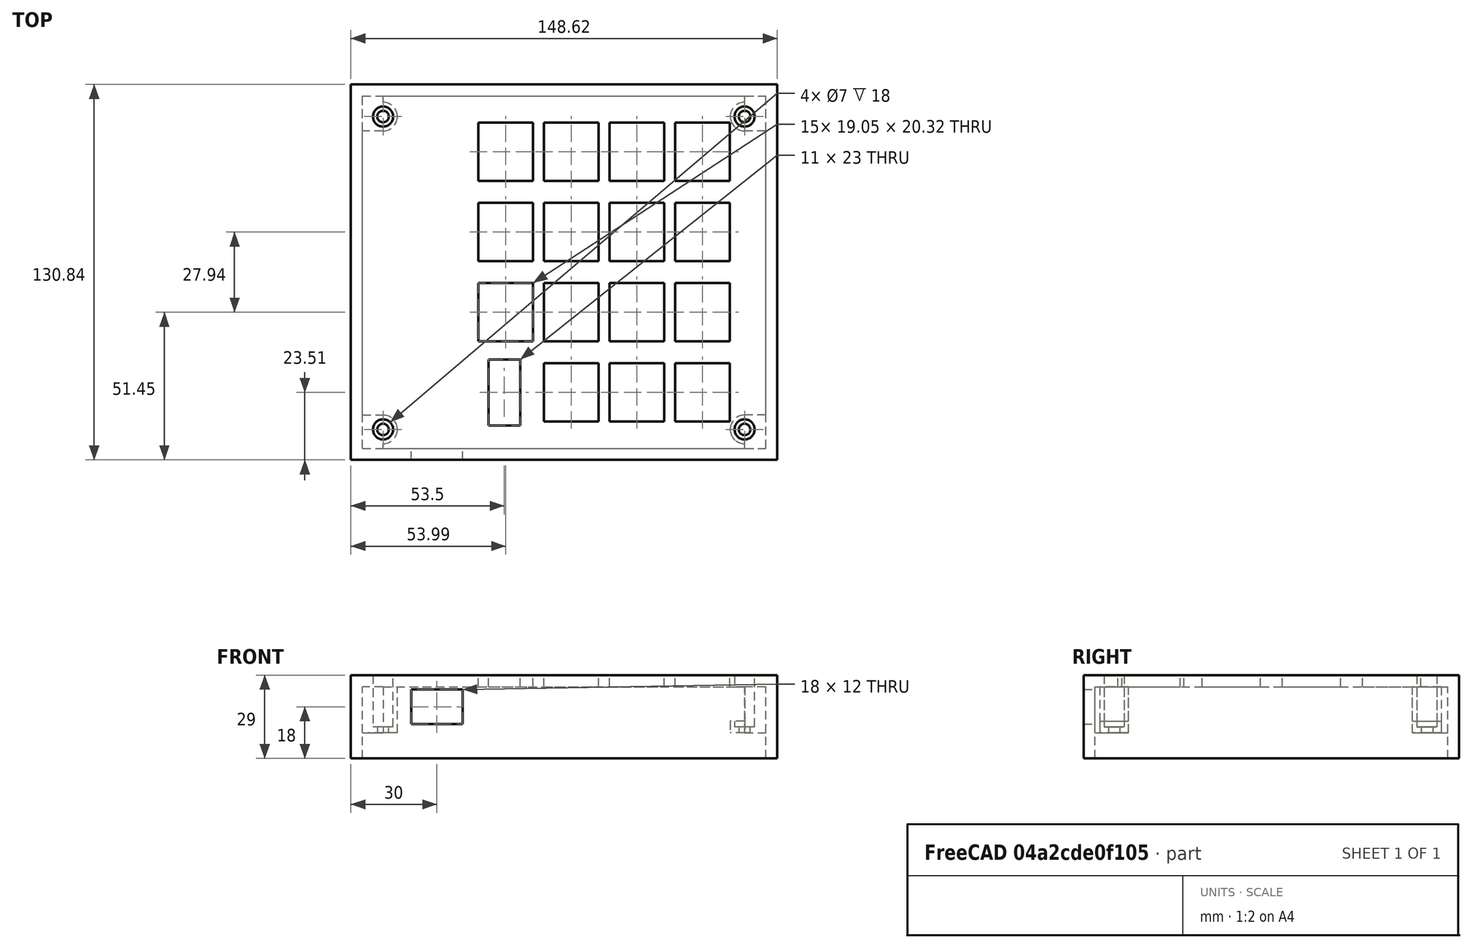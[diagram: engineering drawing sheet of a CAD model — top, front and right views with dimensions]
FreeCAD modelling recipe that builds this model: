
FCSTD DOCUMENT  (FreeCAD 0.20R29410 (Git))
Label: HIDPanelCover
License: All rights reserved
LicenseURL: http://en.wikipedia.org/wiki/All_rights_reserved
objects: Part::Box×25, Part::Cylinder×12, Part::Cut×2, Part::MultiFuse×2, Spreadsheet::Sheet×1
note: 41 computed .brp shape members not serialized (recipe doc carries the construction recipe); baked Part::Feature solids carry a one-line shape summary decoded from their .brp

FEATURE [Spreadsheet::Sheet] Spreadsheet  label="SS"
  cells = A2=PCBWidth; B2(PCBWidth)==116.84mm; A3=PCBLength; B3(PCBLength)==134.62mm; A4=PCBSpacing; B4(PCBSpacing)==3mm; A5=PCBThickness; B5(PCBThickness)==1.6mm; A6=CoverHeight; B6(CoverHeight)==25mm; A7=CaseThickness; B7(CaseThickness)==4mm; A9=StandOffOD; B9(StandOffOD)==10mm; A10=StandOffID; B10(StandOffID)==7mm; A11=StandOfHeight; B11(StandOffHeight)==20mm; A12=StandOffHoleDiameter; B12(StandOffHoleDiameter)==4mm; A13=StandOffBottomThickness; B13(StandOffBottomThickness)==2mm; A15=StandOff1X; B15(StandOff1X)==22mm - 17.78mm; A16=StandOff1Y; B16(StandOff1Y)==90mm - 86.36mm; A17=StandOff2X; B17(StandOff2X)==22mm - 17.78mm; A18=StandOff2Y; B18(StandOff2Y)==199mm - 86.36mm; A19=StandOff3X; B19(StandOff3X)==130.2mm; A20=StandOff3Y; B20(StandOff3Y)==3.64mm; A21=StandOff4X; B21(StandOff4X)==130.2mm; A22=StandOff4Y; B22(StandOff4Y)==112.64mm; A24=CutOut1CtrX; B24(CutOut1CtrX)==87.63mm - 17.78mm; A25=CutOut1CtrY; B25(CutOut1CtrY)==102.87mm - 86.36mm; A26=CutOut1Width; B26(CutOut1Width)==113.03mm - 92.70999999999999mm; A27=CutOut1Length; B27(CutOut1Length)==96.52mm - 77.47mm; A29=CutOut2CtrX; B29(CutOut2CtrX)==110.49mm - 17.78mm; A30=CutOut2CtrY; B30(CutOut2CtrY)==102.87mm - 86.36mm; A31=CutOut2Width; B31(CutOut2Width)==113.03mm - 92.70999999999999mm; A32=CutOut2Length; B32(CutOut2Length)==96.52mm - 77.47mm; A34=CutOut3CtrX; B34(CutOut3CtrX)==133.35mm - 17.78mm; A35=CutOut3CtrY; B35(CutOut3CtrY)==102.87mm - 86.36mm; A36=CutOut3Width; B36(CutOut3Width)==113.03mm - 92.70999999999999mm; A37=CutOut3Length; B37(CutOut3Length)==96.52mm - 77.47mm; A39=CutOut4CtrX; B39(CutOut4CtrX)==64.77mm - 17.78mm; A40=CutOut4CtrY; B40(CutOut4CtrY)==130.81mm - 86.36mm; A41=CutOut4Width; B41(CutOut4Width)==113.03mm - 92.70999999999999mm; A42=CutOut4Length; B42(CutOut4Length)==96.52mm - 77.47mm; A44=CutOut5CtrX; B44(CutOut5CtrX)==87.63mm - 17.78mm; A45=CutOut5CtrY; B45(CutOut5CtrY)==130.81mm - 86.36mm; A46=CutOut5Width; B46(CutOut5Width)==113.03mm - 92.70999999999999mm; A47=CutOut5Length; B47(CutOut5Length)==96.52mm - 77.47mm; A49=CutOut6CtrX; B49(CutOut6CtrX)==110.49mm - 17.78mm; A50=CutOut6CtrY; B50(CutOut6CtrY)==130.81mm - 86.36mm; A51=CutOut6Width; B51(CutOut6Width)==113.03mm - 92.70999999999999mm; A52=CutOut6Length; B52(CutOut6Length)==96.52mm - 77.47mm; A54=CutOut7CtrX; B54(CutOut7CtrX)==133.35mm - 17.78mm; A55=CutOut7CtrY; B55(CutOut7CtrY)==130.81mm - 86.36mm; A56=CutOut7Width; B56(CutOut7Width)==113.03mm - 92.70999999999999mm; A57=CutOut7Length; B57(CutOut7Length)==96.52mm - 77.47mm; A59=CutOut8CtrX; B59(CutOut8CtrX)==64.77mm - 17.78mm; A60=CutOut8CtrY; B60(CutOut8CtrY)==158.75mm - 86.36mm; A61=CutOut8Width; B61(CutOut8Width)==113.03mm - 92.70999999999999mm; A62=CutOut8Length; B62(CutOut8Length)==96.52mm - 77.47mm; A64=CutOut9CtrX; B64(CutOut9CtrX)==87.63mm - 17.78mm; A65=CutOut9CtrY; B65(CutOut9CtrY)==158.75mm - 86.36mm; A66=CutOut9Width; B66(CutOut9Width)==113.03mm - 92.70999999999999mm; A67=CutOut9Length; B67(CutOut9Length)==96.52mm - 77.47mm; A69=CutOut10CtrX; B69(CutOut10CtrX)==110.49mm - 17.78mm; A70=CutOut10CtrY; B70(CutOut10CtrY)==158.75mm - 86.36mm; A71=CutOut10Width; B71(CutOut10Width)==113.03mm - 92.70999999999999mm; A72=CutOut10Length; B72(CutOut10Length)==96.52mm - 77.47mm; A74=CutOut11CtrX; B74(CutOut11CtrX)==133.35mm - 17.78mm; A75=CutOut11CtrY; B75(CutOut11CtrY)==158.75mm - 86.36mm; A76=CutOut11Width; B76(CutOut11Width)==113.03mm - 92.70999999999999mm; A77=CutOut11Length; B77(CutOut11Length)==96.52mm - 77.47mm; A79=CutOut12CtrX; B79(CutOut12CtrX)==64.77mm - 17.78mm; A80=CutOut12CtrY; B80(CutOut12CtrY)==186.69mm - 86.36mm; A81=CutOut12Width; B81(CutOut12Width)==113.03mm - 92.70999999999999mm; A82=CutOut12Length; B82(CutOut12Length)==96.52mm - 77.47mm; A84=CutOut13CtrX; B84(CutOut13CtrX)==87.63mm - 17.78mm; A85=CutOut13CtrY; B85(CutOut13CtrY)==186.69mm - 86.36mm; A86=CutOut13Width; B86(CutOut13Width)==113.03mm - 92.70999999999999mm; A87=CutOut13Length; B87(CutOut13Length)==96.52mm - 77.47mm; A89=CutOut14CtrX; B89(CutOut14CtrX)==110.49mm - 17.78mm; A90=CutOut14CtrY; B90(CutOut14CtrY)==186.69mm - 86.36mm; A91=CutOut14Width; B91(CutOut14Width)==113.03mm - 92.70999999999999mm; A92=CutOut14Length; B92(CutOut14Length)==96.52mm - 77.47mm; A94=CutOut15CtrX; B94(CutOut15CtrX)==133.35mm - 17.78mm; A95=CutOut15CtrY; B95(CutOut15CtrY)==186.69mm - 86.36mm; A96=CutOut15Width; B96(CutOut15Width)==113.03mm - 92.70999999999999mm; A97=CutOut15Length; B97(CutOut15Length)==96.52mm - 77.47mm; A99=LEDCutOutCtrX; B99(LEDCutOutCtrX)==46.5mm; A100=LEDCutOutCtrY; B100(LEDCutOutCtrY)==16.51mm; A101=LEDCutOutWidth; B101(LEDCutOutWidth)==23mm; A102=LEDCutOutLength; B102(LEDCutOutLength)==11mm; A104=CableCutOutZ; B104(CableCutOutZ)==18mm; A105=CableCutOutX; B105(CableCutOutX)==23mm; A106=CableCutOutHeight; B106(CableCutOutHeight)==12mm; A107=CableCutOutLength; B107(CableCutOutLength)==18mm
FEATURE [Part::Box] Box  label="BodyBulk"
  AttacherType = Attacher::AttachEngine3D
  Height = 29
  Length = 148.62
  Placement = pos=(-7,-7,-25) rot=(0,0,1;0rad)
  Width = 130.84
  expr: .Placement.Base.x = -<<SS>>.CaseThickness - <<SS>>.PCBSpacing
  expr: .Placement.Base.y = -<<SS>>.CaseThickness - <<SS>>.PCBSpacing
  expr: .Placement.Base.z = -<<SS>>.CoverHeight
  expr: Height = <<SS>>.CoverHeight + <<SS>>.CaseThickness
  expr: Length = <<SS>>.PCBLength + 2 * (<<SS>>.CaseThickness + <<SS>>.PCBSpacing)
  expr: Width = <<SS>>.PCBWidth + 2 * (<<SS>>.CaseThickness + <<SS>>.PCBSpacing)
FEATURE [Part::Box] Box001  label="BodyInside"
  AttacherType = Attacher::AttachEngine3D
  Height = 25
  Length = 140.62
  Placement = pos=(-3,-3,-25) rot=(0,0,1;0rad)
  Width = 122.84
  expr: .Placement.Base.x = -<<SS>>.PCBSpacing
  expr: .Placement.Base.y = -<<SS>>.PCBSpacing
  expr: .Placement.Base.z = -<<SS>>.CoverHeight
  expr: Height = <<SS>>.CoverHeight
  expr: Length = <<SS>>.PCBLength + 2 * <<SS>>.PCBSpacing
  expr: Width = <<SS>>.PCBWidth + 2 * <<SS>>.PCBSpacing
FEATURE [Part::Cut] Cut  label="BoxWall"
  Base = -> Box
  Tool = -> Box001
FEATURE [Part::Cylinder] Cylinder  label="StandOff1Hole"
  Angle = 360
  AttacherType = Attacher::AttachEngine3D
  FirstAngle = 0
  Height = 20
  Placement = pos=(4.22,3.64,-16) rot=(0,0,1;0rad)
  Radius = 2
  SecondAngle = 0
  expr: .Placement.Base.x = <<SS>>.StandOff1X
  expr: .Placement.Base.y = <<SS>>.StandOff1Y
  expr: .Placement.Base.z = <<SS>>.CaseThickness - <<SS>>.StandOffHeight
  expr: Height = <<SS>>.StandOffHeight
  expr: Radius = <<SS>>.StandOffHoleDiameter / 2
FEATURE [Part::Cylinder] Cylinder001  label="StandOff1ID"
  Angle = 360
  AttacherType = Attacher::AttachEngine3D
  FirstAngle = 0
  Height = 18
  Placement = pos=(4.22,3.64,-14) rot=(0,0,1;0rad)
  Radius = 3.5
  SecondAngle = 0
  expr: .Placement.Base.x = <<SS>>.StandOff1X
  expr: .Placement.Base.y = <<SS>>.StandOff1Y
  expr: .Placement.Base.z = <<SS>>.CaseThickness - <<SS>>.StandOffHeight + <<SS>>.StandOffBottomThickness
  expr: Height = <<SS>>.StandOffHeight - <<SS>>.StandOffBottomThickness
  expr: Radius = <<SS>>.StandOffID / 2
FEATURE [Part::Cylinder] Cylinder002  label="StandOff1OD"
  Angle = 360
  AttacherType = Attacher::AttachEngine3D
  FirstAngle = 0
  Height = 20
  Placement = pos=(4.22,3.64,-16) rot=(0,0,1;0rad)
  Radius = 5
  SecondAngle = 0
  expr: .Placement.Base.x = <<SS>>.StandOff1X
  expr: .Placement.Base.y = <<SS>>.StandOff1Y
  expr: .Placement.Base.z = <<SS>>.CaseThickness - <<SS>>.StandOffHeight
  expr: Height = <<SS>>.StandOffHeight
  expr: Radius = <<SS>>.StandOffOD / 2
FEATURE [Part::Cylinder] Cylinder003  label="StandOff2OD"
  Angle = 360
  AttacherType = Attacher::AttachEngine3D
  FirstAngle = 0
  Height = 20
  Placement = pos=(4.22,112.64,-16) rot=(0,0,1;0rad)
  Radius = 5
  SecondAngle = 0
  expr: .Placement.Base.x = <<SS>>.StandOff2X
  expr: .Placement.Base.y = <<SS>>.StandOff2Y
  expr: .Placement.Base.z = <<SS>>.CaseThickness - <<SS>>.StandOffHeight
  expr: Height = <<SS>>.StandOffHeight
  expr: Radius = <<SS>>.StandOffOD / 2
FEATURE [Part::Cylinder] Cylinder004  label="StandOff2Hole"
  Angle = 360
  AttacherType = Attacher::AttachEngine3D
  FirstAngle = 0
  Height = 20
  Placement = pos=(4.22,112.64,-16) rot=(0,0,1;0rad)
  Radius = 2
  SecondAngle = 0
  expr: .Placement.Base.x = <<SS>>.StandOff2X
  expr: .Placement.Base.y = <<SS>>.StandOff2Y
  expr: .Placement.Base.z = <<SS>>.CaseThickness - <<SS>>.StandOffHeight
  expr: Height = <<SS>>.StandOffHeight
  expr: Radius = <<SS>>.StandOffHoleDiameter / 2
FEATURE [Part::Cylinder] Cylinder005  label="StandOff2ID"
  Angle = 360
  AttacherType = Attacher::AttachEngine3D
  FirstAngle = 0
  Height = 18
  Placement = pos=(4.22,112.64,-14) rot=(0,0,1;0rad)
  Radius = 3.5
  SecondAngle = 0
  expr: .Placement.Base.x = <<SS>>.StandOff2X
  expr: .Placement.Base.y = <<SS>>.StandOff2Y
  expr: .Placement.Base.z = <<SS>>.CaseThickness - <<SS>>.StandOffHeight + <<SS>>.StandOffBottomThickness
  expr: Height = <<SS>>.StandOffHeight - <<SS>>.StandOffBottomThickness
  expr: Radius = <<SS>>.StandOffID / 2
FEATURE [Part::Box] Box004  label="ControlCutOut1"
  AttacherType = Attacher::AttachEngine3D
  Height = 4
  Length = 19.05
  Placement = pos=(60.325,6.35,0) rot=(0,0,1;0rad)
  Width = 20.32
  expr: .Placement.Base.x = <<SS>>.CutOut1CtrX - <<SS>>.CutOut1Length / 2
  expr: .Placement.Base.y = <<SS>>.CutOut1CtrY - <<SS>>.CutOut1Width / 2
  expr: .Placement.Base.z = 0mm
  expr: Height = <<SS>>.CaseThickness
  expr: Length = <<SS>>.CutOut1Length
  expr: Width = <<SS>>.CutOut1Width
FEATURE [Part::Box] Box005  label="ControlCutOut2"
  AttacherType = Attacher::AttachEngine3D
  Height = 4
  Length = 19.05
  Placement = pos=(83.185,6.35,0) rot=(0,0,1;0rad)
  Width = 20.32
  expr: .Placement.Base.x = <<SS>>.CutOut2CtrX - <<SS>>.CutOut2Length / 2
  expr: .Placement.Base.y = <<SS>>.CutOut2CtrY - <<SS>>.CutOut2Width / 2
  expr: .Placement.Base.z = 0mm
  expr: Height = <<SS>>.CaseThickness
  expr: Length = <<SS>>.CutOut2Length
  expr: Width = <<SS>>.CutOut2Width
FEATURE [Part::Box] Box006  label="ControlCutOut3"
  AttacherType = Attacher::AttachEngine3D
  Height = 4
  Length = 19.05
  Placement = pos=(106.045,6.35,0) rot=(0,0,1;0rad)
  Width = 20.32
  expr: .Placement.Base.x = <<SS>>.CutOut3CtrX - <<SS>>.CutOut3Length / 2
  expr: .Placement.Base.y = <<SS>>.CutOut3CtrY - <<SS>>.CutOut3Width / 2
  expr: .Placement.Base.z = 0mm
  expr: Height = <<SS>>.CaseThickness
  expr: Length = <<SS>>.CutOut3Length
  expr: Width = <<SS>>.CutOut3Width
FEATURE [Part::Box] Box007  label="ControlCutOut4"
  AttacherType = Attacher::AttachEngine3D
  Height = 4
  Length = 19.05
  Placement = pos=(37.465,34.29,0) rot=(0,0,1;0rad)
  Width = 20.32
  expr: .Placement.Base.x = <<SS>>.CutOut4CtrX - <<SS>>.CutOut4Length / 2
  expr: .Placement.Base.y = <<SS>>.CutOut4CtrY - <<SS>>.CutOut4Width / 2
  expr: .Placement.Base.z = 0mm
  expr: Height = <<SS>>.CaseThickness
  expr: Length = <<SS>>.CutOut4Length
  expr: Width = <<SS>>.CutOut4Width
FEATURE [Part::Box] Box008  label="ControlCutOut5"
  AttacherType = Attacher::AttachEngine3D
  Height = 4
  Length = 19.05
  Placement = pos=(60.325,34.29,0) rot=(0,0,1;0rad)
  Width = 20.32
  expr: .Placement.Base.x = <<SS>>.CutOut5CtrX - <<SS>>.CutOut5Length / 2
  expr: .Placement.Base.y = <<SS>>.CutOut5CtrY - <<SS>>.CutOut5Width / 2
  expr: .Placement.Base.z = 0mm
  expr: Height = <<SS>>.CaseThickness
  expr: Length = <<SS>>.CutOut5Length
  expr: Width = <<SS>>.CutOut5Width
FEATURE [Part::Box] Box009  label="ControlCutOut6"
  AttacherType = Attacher::AttachEngine3D
  Height = 4
  Length = 19.05
  Placement = pos=(83.185,34.29,0) rot=(0,0,1;0rad)
  Width = 20.32
  expr: .Placement.Base.x = <<SS>>.CutOut6CtrX - <<SS>>.CutOut6Length / 2
  expr: .Placement.Base.y = <<SS>>.CutOut6CtrY - <<SS>>.CutOut6Width / 2
  expr: .Placement.Base.z = 0mm
  expr: Height = <<SS>>.CaseThickness
  expr: Length = <<SS>>.CutOut6Length
  expr: Width = <<SS>>.CutOut6Width
FEATURE [Part::Box] Box010  label="ControlCutOut7"
  AttacherType = Attacher::AttachEngine3D
  Height = 4
  Length = 19.05
  Placement = pos=(106.045,34.29,0) rot=(0,0,1;0rad)
  Width = 20.32
  expr: .Placement.Base.x = <<SS>>.CutOut7CtrX - <<SS>>.CutOut7Length / 2
  expr: .Placement.Base.y = <<SS>>.CutOut7CtrY - <<SS>>.CutOut7Width / 2
  expr: .Placement.Base.z = 0mm
  expr: Height = <<SS>>.CaseThickness
  expr: Length = <<SS>>.CutOut7Length
  expr: Width = <<SS>>.CutOut7Width
FEATURE [Part::Box] Box011  label="ControlCutOut8"
  AttacherType = Attacher::AttachEngine3D
  Height = 4
  Length = 19.05
  Placement = pos=(37.465,62.23,0) rot=(0,0,1;0rad)
  Width = 20.32
  expr: .Placement.Base.x = <<SS>>.CutOut8CtrX - <<SS>>.CutOut8Length / 2
  expr: .Placement.Base.y = <<SS>>.CutOut8CtrY - <<SS>>.CutOut8Width / 2
  expr: .Placement.Base.z = 0mm
  expr: Height = <<SS>>.CaseThickness
  expr: Length = <<SS>>.CutOut8Length
  expr: Width = <<SS>>.CutOut8Width
FEATURE [Part::Box] Box012  label="ControlCutOut9"
  AttacherType = Attacher::AttachEngine3D
  Height = 4
  Length = 19.05
  Placement = pos=(60.325,62.23,0) rot=(0,0,1;0rad)
  Width = 20.32
  expr: .Placement.Base.x = <<SS>>.CutOut9CtrX - <<SS>>.CutOut9Length / 2
  expr: .Placement.Base.y = <<SS>>.CutOut9CtrY - <<SS>>.CutOut9Width / 2
  expr: .Placement.Base.z = 0mm
  expr: Height = <<SS>>.CaseThickness
  expr: Length = <<SS>>.CutOut9Length
  expr: Width = <<SS>>.CutOut9Width
FEATURE [Part::Box] Box013  label="ControlCutOut10"
  AttacherType = Attacher::AttachEngine3D
  Height = 4
  Length = 19.05
  Placement = pos=(83.185,62.23,0) rot=(0,0,1;0rad)
  Width = 20.32
  expr: .Placement.Base.x = <<SS>>.CutOut10CtrX - <<SS>>.CutOut10Length / 2
  expr: .Placement.Base.y = <<SS>>.CutOut10CtrY - <<SS>>.CutOut10Width / 2
  expr: .Placement.Base.z = 0mm
  expr: Height = <<SS>>.CaseThickness
  expr: Length = <<SS>>.CutOut10Length
  expr: Width = <<SS>>.CutOut10Width
FEATURE [Part::Box] Box014  label="ControlCutOut11"
  AttacherType = Attacher::AttachEngine3D
  Height = 4
  Length = 19.05
  Placement = pos=(106.045,62.23,0) rot=(0,0,1;0rad)
  Width = 20.32
  expr: .Placement.Base.x = <<SS>>.CutOut11CtrX - <<SS>>.CutOut11Length / 2
  expr: .Placement.Base.y = <<SS>>.CutOut11CtrY - <<SS>>.CutOut11Width / 2
  expr: .Placement.Base.z = 0mm
  expr: Height = <<SS>>.CaseThickness
  expr: Length = <<SS>>.CutOut11Length
  expr: Width = <<SS>>.CutOut11Width
FEATURE [Part::Box] Box015  label="ControlCutOut12"
  AttacherType = Attacher::AttachEngine3D
  Height = 4
  Length = 19.05
  Placement = pos=(37.465,90.17,0) rot=(0,0,1;0rad)
  Width = 20.32
  expr: .Placement.Base.x = <<SS>>.CutOut12CtrX - <<SS>>.CutOut12Length / 2
  expr: .Placement.Base.y = <<SS>>.CutOut12CtrY - <<SS>>.CutOut12Width / 2
  expr: .Placement.Base.z = 0mm
  expr: Height = <<SS>>.CaseThickness
  expr: Length = <<SS>>.CutOut12Length
  expr: Width = <<SS>>.CutOut12Width
FEATURE [Part::Box] Box016  label="ControlCutOut13"
  AttacherType = Attacher::AttachEngine3D
  Height = 4
  Length = 19.05
  Placement = pos=(60.325,90.17,0) rot=(0,0,1;0rad)
  Width = 20.32
  expr: .Placement.Base.x = <<SS>>.CutOut13CtrX - <<SS>>.CutOut13Length / 2
  expr: .Placement.Base.y = <<SS>>.CutOut13CtrY - <<SS>>.CutOut13Width / 2
  expr: .Placement.Base.z = 0mm
  expr: Height = <<SS>>.CaseThickness
  expr: Length = <<SS>>.CutOut13Length
  expr: Width = <<SS>>.CutOut13Width
FEATURE [Part::Box] Box017  label="ControlCutOut14"
  AttacherType = Attacher::AttachEngine3D
  Height = 4
  Length = 19.05
  Placement = pos=(83.185,90.17,0) rot=(0,0,1;0rad)
  Width = 20.32
  expr: .Placement.Base.x = <<SS>>.CutOut14CtrX - <<SS>>.CutOut14Length / 2
  expr: .Placement.Base.y = <<SS>>.CutOut14CtrY - <<SS>>.CutOut14Width / 2
  expr: .Placement.Base.z = 0mm
  expr: Height = <<SS>>.CaseThickness
  expr: Length = <<SS>>.CutOut14Length
  expr: Width = <<SS>>.CutOut14Width
FEATURE [Part::Box] Box018  label="ControlCutOut15"
  AttacherType = Attacher::AttachEngine3D
  Height = 4
  Length = 19.05
  Placement = pos=(106.045,90.17,0) rot=(0,0,1;0rad)
  Width = 20.32
  expr: .Placement.Base.x = <<SS>>.CutOut15CtrX - <<SS>>.CutOut15Length / 2
  expr: .Placement.Base.y = <<SS>>.CutOut15CtrY - <<SS>>.CutOut15Width / 2
  expr: .Placement.Base.z = 0mm
  expr: Height = <<SS>>.CaseThickness
  expr: Length = <<SS>>.CutOut15Length
  expr: Width = <<SS>>.CutOut15Width
FEATURE [Part::Box] Box019  label="LEDCutOut"
  AttacherType = Attacher::AttachEngine3D
  Height = 4
  Length = 11
  Placement = pos=(41,5.01,0) rot=(0,0,1;0rad)
  Width = 23
  expr: .Placement.Base.x = <<SS>>.LEDCutOutCtrX - <<SS>>.LEDCutOutLength / 2
  expr: .Placement.Base.y = <<SS>>.LEDCutOutCtrY - <<SS>>.LEDCutOutWidth / 2
  expr: .Placement.Base.z = 0mm
  expr: Height = <<SS>>.CaseThickness
  expr: Length = <<SS>>.LEDCutOutLength
  expr: Width = <<SS>>.LEDCutOutWidth
FEATURE [Part::Cylinder] Cylinder006  label="StandOff3OD"
  Angle = 360
  AttacherType = Attacher::AttachEngine3D
  FirstAngle = 0
  Height = 20
  Placement = pos=(130.2,3.64,-16) rot=(0,0,1;0rad)
  Radius = 5
  SecondAngle = 0
  expr: .Placement.Base.x = <<SS>>.StandOff3X
  expr: .Placement.Base.y = <<SS>>.StandOff3Y
  expr: .Placement.Base.z = <<SS>>.CaseThickness - <<SS>>.StandOffHeight
  expr: Height = <<SS>>.StandOffHeight
  expr: Radius = <<SS>>.StandOffOD / 2
FEATURE [Part::Cylinder] Cylinder007  label="StandOff4OD"
  Angle = 360
  AttacherType = Attacher::AttachEngine3D
  FirstAngle = 0
  Height = 20
  Placement = pos=(130.2,112.64,-16) rot=(0,0,1;0rad)
  Radius = 5
  SecondAngle = 0
  expr: .Placement.Base.x = <<SS>>.StandOff4X
  expr: .Placement.Base.y = <<SS>>.StandOff4Y
  expr: .Placement.Base.z = <<SS>>.CaseThickness - <<SS>>.StandOffHeight
  expr: Height = <<SS>>.StandOffHeight
  expr: Radius = <<SS>>.StandOffOD / 2
FEATURE [Part::Cylinder] Cylinder008  label="StandOff3Hole"
  Angle = 360
  AttacherType = Attacher::AttachEngine3D
  FirstAngle = 0
  Height = 20
  Placement = pos=(130.2,3.64,-16) rot=(0,0,1;0rad)
  Radius = 2
  SecondAngle = 0
  expr: .Placement.Base.x = <<SS>>.StandOff3X
  expr: .Placement.Base.y = <<SS>>.StandOff3Y
  expr: .Placement.Base.z = <<SS>>.CaseThickness - <<SS>>.StandOffHeight
  expr: Height = <<SS>>.StandOffHeight
  expr: Radius = <<SS>>.StandOffHoleDiameter / 2
FEATURE [Part::Cylinder] Cylinder009  label="StandOff4Hole"
  Angle = 360
  AttacherType = Attacher::AttachEngine3D
  FirstAngle = 0
  Height = 20
  Placement = pos=(130.2,112.64,-16) rot=(0,0,1;0rad)
  Radius = 2
  SecondAngle = 0
  expr: .Placement.Base.x = <<SS>>.StandOff4X
  expr: .Placement.Base.y = <<SS>>.StandOff4Y
  expr: .Placement.Base.z = <<SS>>.CaseThickness - <<SS>>.StandOffHeight
  expr: Height = <<SS>>.StandOffHeight
  expr: Radius = <<SS>>.StandOffHoleDiameter / 2
FEATURE [Part::Cylinder] Cylinder010  label="StandOff3ID"
  Angle = 360
  AttacherType = Attacher::AttachEngine3D
  FirstAngle = 0
  Height = 18
  Placement = pos=(130.2,3.64,-14) rot=(0,0,1;0rad)
  Radius = 3.5
  SecondAngle = 0
  expr: .Placement.Base.x = <<SS>>.StandOff3X
  expr: .Placement.Base.y = <<SS>>.StandOff3Y
  expr: .Placement.Base.z = <<SS>>.CaseThickness - <<SS>>.StandOffHeight + <<SS>>.StandOffBottomThickness
  expr: Height = <<SS>>.StandOffHeight - <<SS>>.StandOffBottomThickness
  expr: Radius = <<SS>>.StandOffID / 2
FEATURE [Part::Cylinder] Cylinder011  label="StandOff4ID"
  Angle = 360
  AttacherType = Attacher::AttachEngine3D
  FirstAngle = 0
  Height = 18
  Placement = pos=(130.2,112.64,-14) rot=(0,0,1;0rad)
  Radius = 3.5
  SecondAngle = 0
  expr: .Placement.Base.x = <<SS>>.StandOff4X
  expr: .Placement.Base.y = <<SS>>.StandOff4Y
  expr: .Placement.Base.z = <<SS>>.CaseThickness - <<SS>>.StandOffHeight + <<SS>>.StandOffBottomThickness
  expr: Height = <<SS>>.StandOffHeight - <<SS>>.StandOffBottomThickness
  expr: Radius = <<SS>>.StandOffID / 2
FEATURE [Part::Box] Box020  label="CableCutOut"
  AttacherType = Attacher::AttachEngine3D
  Height = 12
  Length = 18
  Placement = pos=(14,-7,-13) rot=(0,0,1;0rad)
  Width = 4
  expr: .Placement.Base.x = <<SS>>.CableCutOutX - <<SS>>.CableCutOutLength / 2
  expr: .Placement.Base.y = -<<SS>>.CaseThickness - <<SS>>.PCBSpacing
  expr: .Placement.Base.z = -<<SS>>.CoverHeight + <<SS>>.CableCutOutZ - <<SS>>.CableCutOutHeight / 2
  expr: Height = <<SS>>.CableCutOutHeight
  expr: Length = <<SS>>.CableCutOutLength
  expr: Width = <<SS>>.CaseThickness
FEATURE [Part::Box] Box021  label="StandOff3Remove"
  AttacherType = Attacher::AttachEngine3D
  Height = 12
  Length = 5
  Placement = pos=(125.2,-1.36,-12) rot=(0,0,1;0rad)
  Width = 10
  expr: .Placement.Base.x = <<SS>>.StandOff3X - <<SS>>.StandOffOD / 2
  expr: .Placement.Base.y = <<SS>>.StandOff3Y - <<SS>>.StandOffOD / 2
  expr: .Placement.Base.z = -<<SS>>.StandOffHeight + 2 * <<SS>>.CaseThickness
  expr: Height = <<SS>>.StandOffHeight - 2 * <<SS>>.CaseThickness
  expr: Length = <<SS>>.StandOffOD / 2
  expr: Width = <<SS>>.StandOffOD
FEATURE [Part::Box] Box022  label="StandOff4Remove"
  AttacherType = Attacher::AttachEngine3D
  Height = 12
  Length = 5
  Placement = pos=(125.2,107.64,-12) rot=(0,0,1;0rad)
  Width = 10
  expr: .Placement.Base.x = <<SS>>.StandOff4X - <<SS>>.StandOffOD / 2
  expr: .Placement.Base.y = <<SS>>.StandOff4Y - <<SS>>.StandOffOD / 2
  expr: .Placement.Base.z = -<<SS>>.StandOffHeight + 2 * <<SS>>.CaseThickness
  expr: Height = <<SS>>.StandOffHeight - 2 * <<SS>>.CaseThickness
  expr: Length = <<SS>>.StandOffOD / 2
  expr: Width = <<SS>>.StandOffOD
FEATURE [Part::MultiFuse] Fusion  label="StandOffCutOuts"
  Shapes = -> [Cylinder,Cylinder001,Cylinder004,Cylinder005,Box004,Box005,Box006,Box007,Box008,Box009,Box010,Box011,Box012,Box013,Box014,Box015,Box016,Box017,Box018,Box019,Cylinder008,Cylinder009,Cylinder010,Cylinder011,Box020,Box021,Box022]
FEATURE [Part::Box] Box023  label="StandOff1Attach"
  AttacherType = Attacher::AttachEngine3D
  Height = 20
  Length = 7.22
  Placement = pos=(-3,-3,-16) rot=(0,0,1;0rad)
  Width = 11.64
  expr: .Placement.Base.x = -<<SS>>.PCBSpacing
  expr: .Placement.Base.y = -<<SS>>.PCBSpacing
  expr: .Placement.Base.z = <<SS>>.CaseThickness - <<SS>>.StandOffHeight
  expr: Height = <<SS>>.StandOffHeight
  expr: Length = <<SS>>.StandOff1X + <<SS>>.PCBSpacing
  expr: Width = <<SS>>.StandOff1Y + <<SS>>.PCBSpacing + <<SS>>.StandOffOD / 2
FEATURE [Part::Box] Box024  label="StandOff2Attach"
  AttacherType = Attacher::AttachEngine3D
  Height = 20
  Length = 7.22
  Placement = pos=(-3,107.64,-16) rot=(0,0,1;0rad)
  Width = 12.2
  expr: .Placement.Base.x = -<<SS>>.PCBSpacing
  expr: .Placement.Base.y = <<SS>>.StandOff2Y - <<SS>>.StandOffOD / 2
  expr: .Placement.Base.z = <<SS>>.CaseThickness - <<SS>>.StandOffHeight
  expr: Height = <<SS>>.StandOffHeight
  expr: Length = <<SS>>.StandOff2X + <<SS>>.PCBSpacing
  expr: Width = <<SS>>.PCBWidth - <<SS>>.StandOff2Y + <<SS>>.PCBSpacing + <<SS>>.StandOffOD / 2
FEATURE [Part::Box] Box025  label="StandOff3Attach"
  AttacherType = Attacher::AttachEngine3D
  Height = 20
  Length = 7.42
  Placement = pos=(130.2,-3,-16) rot=(0,0,1;0rad)
  Width = 11.64
  expr: .Placement.Base.x = <<SS>>.StandOff3X
  expr: .Placement.Base.y = -<<SS>>.PCBSpacing
  expr: .Placement.Base.z = <<SS>>.CaseThickness - <<SS>>.StandOffHeight
  expr: Height = <<SS>>.StandOffHeight
  expr: Length = <<SS>>.PCBLength - <<SS>>.StandOff3X + <<SS>>.PCBSpacing
  expr: Width = <<SS>>.StandOff3Y + <<SS>>.PCBSpacing + <<SS>>.StandOffOD / 2
FEATURE [Part::Box] Box026  label="StandOff4Attach"
  AttacherType = Attacher::AttachEngine3D
  Height = 20
  Length = 7.42
  Placement = pos=(130.2,107.64,-16) rot=(0,0,1;0rad)
  Width = 12.2
  expr: .Placement.Base.x = <<SS>>.StandOff4X
  expr: .Placement.Base.y = <<SS>>.StandOff4Y - <<SS>>.StandOffOD / 2
  expr: .Placement.Base.z = <<SS>>.CaseThickness - <<SS>>.StandOffHeight
  expr: Height = <<SS>>.StandOffHeight
  expr: Length = <<SS>>.PCBLength - <<SS>>.StandOff4X + <<SS>>.PCBSpacing
  expr: Width = <<SS>>.PCBWidth - <<SS>>.StandOff4Y + <<SS>>.PCBSpacing + <<SS>>.StandOffOD / 2
FEATURE [Part::MultiFuse] Fusion001  label="BoxWallWithStandoffs"
  Shapes = -> [Cut,Cylinder002,Cylinder003,Cylinder006,Cylinder007,Box023,Box024,Box025,Box026]
FEATURE [Part::Cut] Cut001  label="BoxWithStandOffs"
  Base = -> Fusion001
  Tool = -> Fusion
